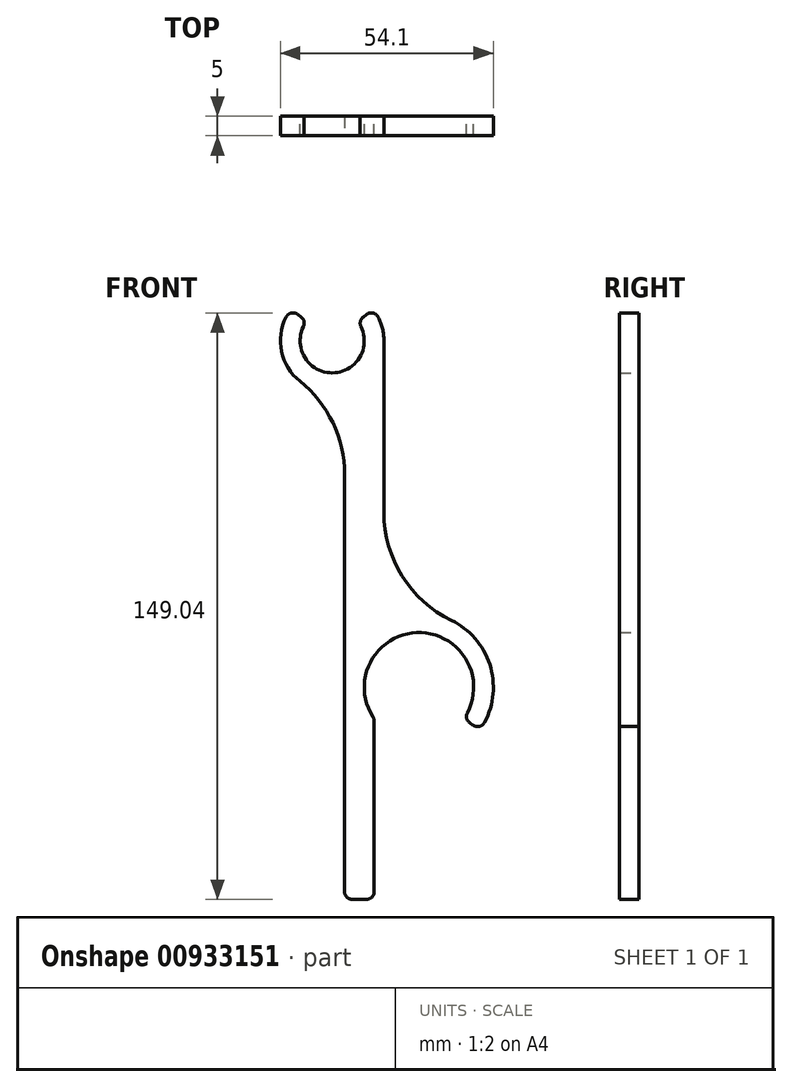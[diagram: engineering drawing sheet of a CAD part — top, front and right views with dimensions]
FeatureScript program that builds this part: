
annotation { "Feature Type Name" : "Feature", "Feature Type Description" : "" }
export const myFeature = defineFeature(function(context is Context, id is Id, definition is map)
    precondition{}
    {
        {
            var Q0;
            Q0=qCreatedBy(makeId("Front.planeOp"),FACE);
            var sketch = newSketch(context, id + "F0", { "sketchPlane" : qUnion([Q0])});
            skPoint(sketch, "E0", {"position": v(35.95, -88.05) * mm});
            skArc(sketch, "E1", {"start": v(-4.78, -12.25) * mm, "mid": v(-0.86, -13.12) * mm, "end": v(3.15, -12.77) * mm});
            skArc(sketch, "E2", {"start": v(-0.44, 13.14) * mm, "mid": v(-12.96, 2.22) * mm, "end": v(-4.78, -12.25) * mm});
            skArc(sketch, "E3", {"start": v(6.57, -98.9) * mm, "mid": v(40.43, -92.45) * mm, "end": v(13.15, -71.38) * mm});
            skLineSegment(sketch, "E4", {"start": v(-10.43, 8) * mm, "end": v(0, 0) * mm});
            skLineSegment(sketch, "E5", {"start": v(0, 0) * mm, "end": v(10.43, 8) * mm});
            skLineSegment(sketch, "E6", {"start": v(22.05, -88.05) * mm, "end": v(6.57, -98.9) * mm});
            skLineSegment(sketch, "E7", {"start": v(22.05, -88.05) * mm, "end": v(37.53, -98.9) * mm});
            skArc(sketch, "E8", {"start": v(6.47, 4.96) * mm, "mid": v(0, 8.15) * mm, "end": v(-6.47, 4.96) * mm});
            skArc(sketch, "E9", {"start": v(-6.47, 4.96) * mm, "mid": v(0, -8.15) * mm, "end": v(6.47, 4.96) * mm});
            skArc(sketch, "E10", {"start": v(10.66, -96.02) * mm, "mid": v(22.05, -101.95) * mm, "end": v(33.44, -96.02) * mm});
            skArc(sketch, "E11", {"start": v(33.44, -96.02) * mm, "mid": v(22.05, -74.15) * mm, "end": v(10.66, -96.02) * mm});
            skArc(sketch, "E12", {"start": v(4.96, -79.98) * mm, "mid": v(3.22, -89.65) * mm, "end": v(6.57, -98.9) * mm});
            skArc(sketch, "E13", {"start": v(8.43, -10.1) * mm, "mid": v(12.29, 4.69) * mm, "end": v(-0.44, 13.14) * mm});
            skPoint(sketch, "E14.visualSharp", {"position": v(8.43, -10.1) * mm});
            skPoint(sketch, "E15", {"position": v(8.15, -88.05) * mm});
            skPoint(sketch, "E16", {"position": v(8.15, 0) * mm});
            skLineSegment(sketch, "E17.top", {"start": v(3.15, -141.95) * mm, "end": v(10.66, -141.95) * mm});
            skLineSegment(sketch, "E17.left", {"start": v(3.15, -88.05) * mm, "end": v(3.15, -141.95) * mm});
            skPoint(sketch, "E18", {"position": v(22.05, -106.95) * mm});
            skPoint(sketch, "E18.positionSnap0", {"position": v(22.05, -101.95) * mm});
            skLineSegment(sketch, "E19.left", {"start": v(13.15, 0) * mm, "end": v(13.15, -71.38) * mm});
            skArc(sketch, "E20", {"start": v(3.15, -12.77) * mm, "mid": v(5.94, -11.73) * mm, "end": v(8.43, -10.1) * mm});
            skArc(sketch, "E21", {"start": v(13.15, -71.38) * mm, "mid": v(8.36, -75.02) * mm, "end": v(4.96, -79.98) * mm});
            skPoint(sketch, "E22", {"position": v(0, -8.15) * mm});
            skPoint(sketch, "E23", {"position": v(22.05, -74.15) * mm});
            skLineSegment(sketch, "E24", {"start": v(3.15, -12.77) * mm, "end": v(3.15, -88.05) * mm});
            skLineSegment(sketch, "E25", {"start": v(10.66, -96.02) * mm, "end": v(10.66, -141.95) * mm});
            skSolve(sketch);
        }
        {
            var Q0;
            {var subQ1=sQuery(id+"F0.wireOp",EDGE,"E19.left");Q0=makeQuery(id+"F0.imprint","IMPRINT",FACE,{"disambiguationData":[TD([[makeQuery(id+"F0.imprint","IMPRINT",EDGE,{"derivedFrom":subQ1}),-1.0]])]});}
            var Q1;
            {var subQ0=sQuery(id+"F0.wireOp",EDGE,"E11");Q1=makeQuery(id+"F0.imprint","IMPRINT",FACE,{"disambiguationData":[TD([[makeQuery(id+"F0.imprint","IMPRINT",EDGE,{"derivedFrom":subQ0}),-1.0]])]});}
            var Q2;
            Q2=makeQuery(id+"F0.imprint","IMPRINT",FACE,{"disambiguationData":[TD([[makeQuery(id+"F0.imprint","IMPRINT",EDGE,{"derivedFrom":sQuery(id+"F0.wireOp",EDGE,"E17.top")}),1.0]])]});
            var Q3;
            {var subQ1=sQuery(id+"F0.wireOp",EDGE,"E3");var subQ3=sQuery(id+"F0.wireOp",EDGE,"E25");var subQ4=makeQuery(id+"F0.imprint","INTERSECT",VERTEX,{"derivedFrom":[subQ1,subQ3]});Q3=makeQuery(id+"F0.imprint","IMPRINT",FACE,{"disambiguationData":[TD([[makeQuery(id+"F0.imprint","IMPRINT",EDGE,{"disambiguationData":[TD([[subQ4,1.0]])],"derivedFrom":subQ1}),1.0]])]});}
            var Q4;
            {var subQ10=sQuery(id+"F0.wireOp",EDGE,"E1");Q4=makeQuery(id+"F0.imprint","IMPRINT",FACE,{"disambiguationData":[TD([[makeQuery(id+"F0.imprint","IMPRINT",EDGE,{"derivedFrom":subQ10}),1.0]])]});}
            extrude(context, id + "F1", {"entities" : qUnion([Q0, Q1, Q2, Q3, Q4]), "depth" : 5 * mm, "offsetDistance" : 25 * mm});
        }
        {
            var Q0;
            Q0=makeQuery(id+"F1.opExtrude","SWEPT_EDGE",EDGE,{"disambiguationData":[OSD([sQuery(id+"F0.wireOp",EDGE,"E2"),sQuery(id+"F0.wireOp",EDGE,"E5")])]});
            var Q1;
            Q1=makeQuery(id+"F1.opExtrude","SWEPT_EDGE",EDGE,{"disambiguationData":[OSD([sQuery(id+"F0.wireOp",EDGE,"E5"),sQuery(id+"F0.wireOp",EDGE,"E8"),sQuery(id+"F0.wireOp",EDGE,"E9")])]});
            var Q2;
            Q2=makeQuery(id+"F1.opExtrude","SWEPT_EDGE",EDGE,{"disambiguationData":[OSD([sQuery(id+"F0.wireOp",EDGE,"E4"),sQuery(id+"F0.wireOp",EDGE,"E8"),sQuery(id+"F0.wireOp",EDGE,"E9")])]});
            var Q3;
            Q3=makeQuery(id+"F1.opExtrude","SWEPT_EDGE",EDGE,{"disambiguationData":[OSD([sQuery(id+"F0.wireOp",EDGE,"E2"),sQuery(id+"F0.wireOp",EDGE,"E4")])]});
            var Q4;
            Q4=makeQuery(id+"F1.opExtrude","SWEPT_EDGE",EDGE,{"disambiguationData":[OSD([sQuery(id+"F0.wireOp",EDGE,"E3"),sQuery(id+"F0.wireOp",EDGE,"680ca464-2a6f-4f87-88b0-3cb272eb12a2.filletArc")])]});
            var Q5;
            Q5=makeQuery(id+"F1.opExtrude","SWEPT_EDGE",EDGE,{"disambiguationData":[OSD([sQuery(id+"F0.wireOp",EDGE,"E6"),sQuery(id+"F0.wireOp",EDGE,"E10"),sQuery(id+"F0.wireOp",EDGE,"E11")])]});
            var Q6;
            Q6=makeQuery(id+"F1.opExtrude","SWEPT_EDGE",EDGE,{"disambiguationData":[OSD([sQuery(id+"F0.wireOp",EDGE,"E7"),sQuery(id+"F0.wireOp",EDGE,"E10"),sQuery(id+"F0.wireOp",EDGE,"E11")])]});
            var Q7;
            Q7=makeQuery(id+"F1.opExtrude","SWEPT_EDGE",EDGE,{"disambiguationData":[OSD([sQuery(id+"F0.wireOp",EDGE,"E3"),sQuery(id+"F0.wireOp",EDGE,"E7")])]});
            var Q8;
            Q8=makeQuery(id+"F1.opExtrude","SWEPT_EDGE",EDGE,{"disambiguationData":[OSD([sQuery(id+"F0.wireOp",EDGE,"E3"),sQuery(id+"F0.wireOp",EDGE,"E6"),sQuery(id+"F0.wireOp",EDGE,"E12")])]});
            var Q9;
            Q9=makeQuery(id+"F1.opExtrude","SWEPT_EDGE",EDGE,{"disambiguationData":[OSD([sQuery(id+"F0.wireOp",EDGE,"E17.top"),sQuery(id+"F0.wireOp",EDGE,"E17.left")])]});
            var Q10;
            Q10=makeQuery(id+"F1.opExtrude","SWEPT_EDGE",EDGE,{"disambiguationData":[OSD([sQuery(id+"F0.wireOp",EDGE,"E17.top"),sQuery(id+"F0.wireOp",EDGE,"E25")])]});
            fillet(context, id + "F2", {"entities" : qUnion([Q0, Q1, Q2, Q3, Q4, Q5, Q6, Q7, Q8, Q9, Q10]), "radius" : 2 * mm, "tangentPropagation" : true, "allowEdgeOverflow" : false});
        }
        {
            var Q0;
            Q0=makeQuery(id+"F1.opExtrude","SWEPT_EDGE",EDGE,{"disambiguationData":[OSD([sQuery(id+"F0.wireOp",EDGE,"E1"),sQuery(id+"F0.wireOp",EDGE,"E20"),sQuery(id+"F0.wireOp",EDGE,"E24")])]});
            var Q1;
            Q1=makeQuery(id+"F1.opExtrude","SWEPT_EDGE",EDGE,{"disambiguationData":[OSD([sQuery(id+"F0.wireOp",EDGE,"E3"),sQuery(id+"F0.wireOp",EDGE,"E19.left"),sQuery(id+"F0.wireOp",EDGE,"E21")])]});
            fillet(context, id + "F3", {"entities" : qUnion([Q0, Q1]), "radius" : 30.4 * mm, "tangentPropagation" : true, "allowEdgeOverflow" : false});
        }
    });
